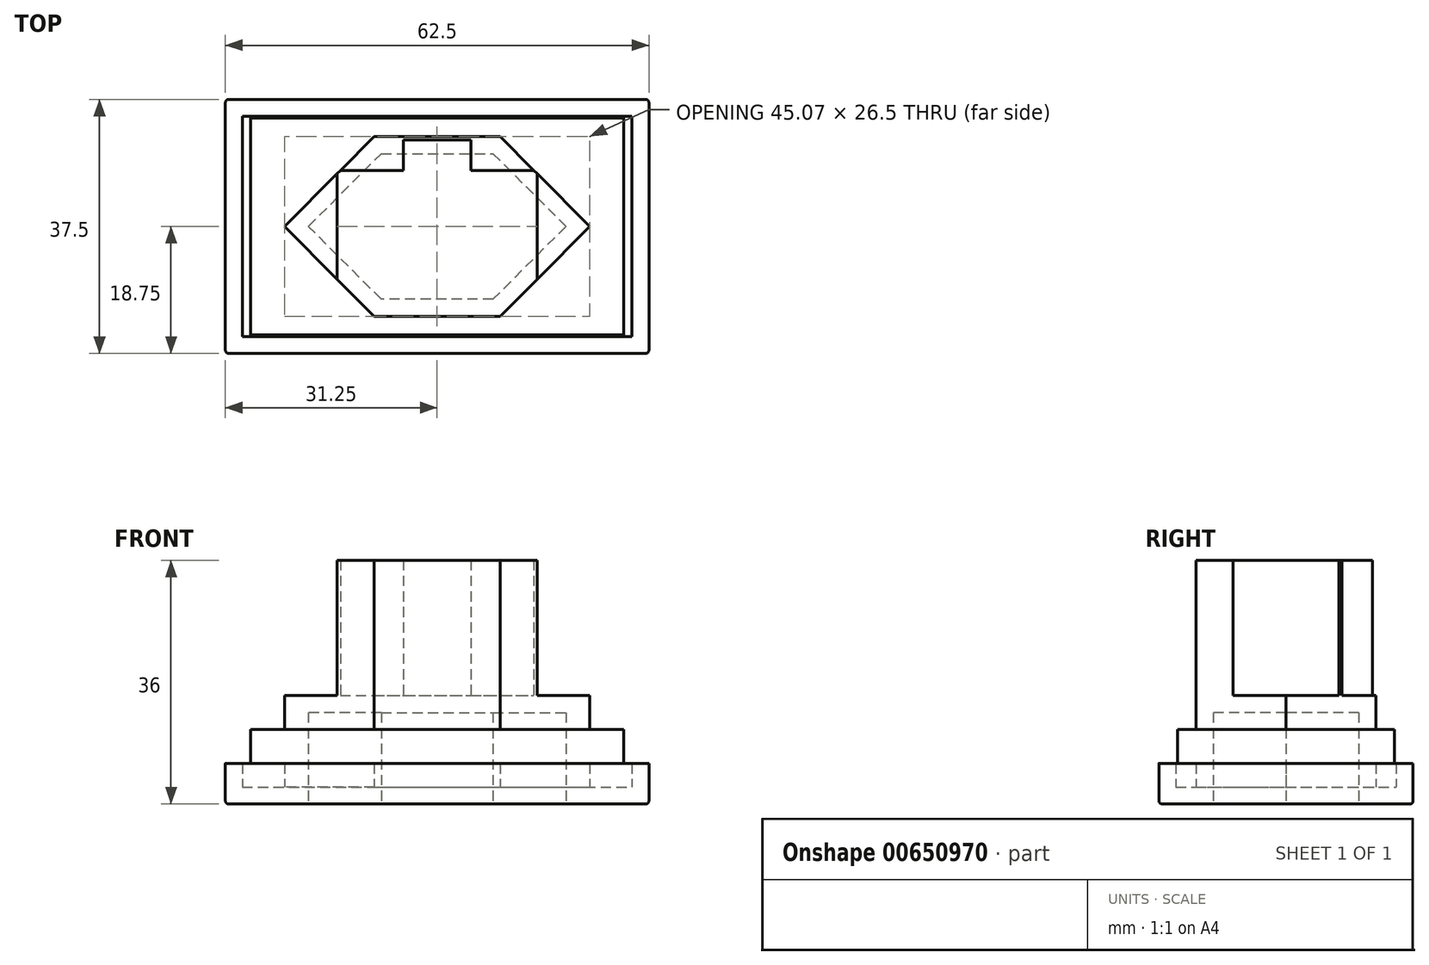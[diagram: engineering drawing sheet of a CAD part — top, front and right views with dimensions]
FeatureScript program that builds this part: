
annotation { "Feature Type Name" : "Feature", "Feature Type Description" : "" }
export const myFeature = defineFeature(function(context is Context, id is Id, definition is map)
    precondition{}
    {
        {
            var Q0;
            Q0=qCreatedBy(makeId("Top.planeOp"),FACE);
            var sketch = newSketch(context, id + "F0", { "sketchPlane" : qUnion([Q0])});
            skLineSegment(sketch, "E0.bottom", {"start": v(0, 0) * mm, "end": v(62.5, 0) * mm});
            skLineSegment(sketch, "E0.top", {"start": v(0, 37.5) * mm, "end": v(62.5, 37.5) * mm});
            skLineSegment(sketch, "E0.left", {"start": v(0, 0) * mm, "end": v(0, 37.5) * mm});
            skLineSegment(sketch, "E0.right", {"start": v(62.5, 0) * mm, "end": v(62.5, 37.5) * mm});
            skLineSegment(sketch, "E1", {"start": v(12.25, 18.75) * mm, "end": v(23, 29.5) * mm});
            skLineSegment(sketch, "E2", {"start": v(23, 29.5) * mm, "end": v(39.5, 29.5) * mm});
            skLineSegment(sketch, "E3", {"start": v(39.5, 29.5) * mm, "end": v(50.25, 18.75) * mm});
            skLineSegment(sketch, "E4", {"start": v(50.25, 18.75) * mm, "end": v(39.5, 8) * mm});
            skLineSegment(sketch, "E5", {"start": v(39.5, 8) * mm, "end": v(23, 8) * mm});
            skLineSegment(sketch, "E6", {"start": v(23, 8) * mm, "end": v(12.25, 18.75) * mm});
            skLineSegment(sketch, "E7", {"start": v(23, 8) * mm, "end": v(23, 29.5) * mm, "construction": true});
            skLineSegment(sketch, "E8", {"start": v(31.25, 29.5) * mm, "end": v(31.25, 8) * mm, "construction": true});
            skLineSegment(sketch, "E9", {"start": v(12.25, 18.75) * mm, "end": v(50.25, 18.75) * mm, "construction": true});
            skSolve(sketch);
        }
        {
            var Q0;
            Q0=makeQuery(id+"F0.imprint","IMPRINT",FACE,{"disambiguationData":[TD([[makeQuery(id+"F0.imprint","IMPRINT",EDGE,{"derivedFrom":sQuery(id+"F0.wireOp",EDGE,"E0.bottom")}),1.0]])]});
            extrude(context, id + "F1", {"entities" : qUnion([Q0]), "depth" : 6 * mm, "offsetDistance" : 25 * mm});
        }
        {
            var Q0;
            Q0=makeQuery(id+"F0.imprint","IMPRINT",FACE,{"disambiguationData":[TD([[makeQuery(id+"F0.imprint","IMPRINT",EDGE,{"derivedFrom":sQuery(id+"F0.wireOp",EDGE,"E1")}),-1.0]])]});
            extrude(context, id + "F2", {"entities" : qUnion([Q0]), "depth" : 13.5 * mm, "offsetDistance" : 25 * mm});
        }
        {
            var Q0;
            Q0=makeQuery(id+"F2.opExtrude","CAP_FACE",FACE,{"disambiguationData":[OSD([sQuery(id+"F0.wireOp",EDGE,"E1"),sQuery(id+"F0.wireOp",EDGE,"E2"),sQuery(id+"F0.wireOp",EDGE,"E3"),sQuery(id+"F0.wireOp",EDGE,"E4"),sQuery(id+"F0.wireOp",EDGE,"E5"),sQuery(id+"F0.wireOp",EDGE,"E6")])],"isStart":true});
            shell(context, id + "F3", {"entities" : qUnion([Q0]), "thickness" : 2.5 * mm, "oppositeDirection" : true});
        }
        {
            var Q0;
            Q0=makeQuery(id+"F1.opExtrude","CAP_FACE",FACE,{"disambiguationData":[OSD([sQuery(id+"F0.wireOp",EDGE,"E0.bottom"),sQuery(id+"F0.wireOp",EDGE,"E0.top"),sQuery(id+"F0.wireOp",EDGE,"E0.left"),sQuery(id+"F0.wireOp",EDGE,"E0.right"),sQuery(id+"F0.wireOp",EDGE,"E1"),sQuery(id+"F0.wireOp",EDGE,"E2"),sQuery(id+"F0.wireOp",EDGE,"E3"),sQuery(id+"F0.wireOp",EDGE,"E4"),sQuery(id+"F0.wireOp",EDGE,"E5"),sQuery(id+"F0.wireOp",EDGE,"E6")])],"isStart":false});
            shell(context, id + "F4", {"entities" : qUnion([Q0]), "thickness" : 2.5 * mm});
        }
        {
            var Q0;
            Q0=makeQuery(id+"F2.opExtrude","CAP_FACE",FACE,{"disambiguationData":[OSD([sQuery(id+"F0.wireOp",EDGE,"E1"),sQuery(id+"F0.wireOp",EDGE,"E2"),sQuery(id+"F0.wireOp",EDGE,"E3"),sQuery(id+"F0.wireOp",EDGE,"E4"),sQuery(id+"F0.wireOp",EDGE,"E5"),sQuery(id+"F0.wireOp",EDGE,"E6")])],"isStart":false});
            var sketch = newSketch(context, id + "F5", { "sketchPlane" : qUnion([Q0])});
            skLineSegment(sketch, "E10.bottom", {"start": v(16.5, 5.5) * mm, "end": v(46, 5.5) * mm});
            skLineSegment(sketch, "E10.left", {"start": v(16.5, 5.5) * mm, "end": v(16.5, 27) * mm});
            skLineSegment(sketch, "E10.right", {"start": v(46, 5.5) * mm, "end": v(46, 27) * mm});
            skLineSegment(sketch, "E11.top", {"start": v(26.25, 31.5) * mm, "end": v(36.25, 31.5) * mm});
            skLineSegment(sketch, "E11.left", {"start": v(26.25, 27) * mm, "end": v(26.25, 31.5) * mm});
            skLineSegment(sketch, "E11.right", {"start": v(36.25, 27) * mm, "end": v(36.25, 31.5) * mm});
            skLineSegment(sketch, "E12", {"start": v(16.5, 27) * mm, "end": v(26.25, 27) * mm});
            skLineSegment(sketch, "E13", {"start": v(36.25, 27) * mm, "end": v(46, 27) * mm});
            skLineSegment(sketch, "E14", {"start": v(31.25, 31.5) * mm, "end": v(31.25, 5.5) * mm, "construction": true});
            skSolve(sketch);
        }
        {
            var Q0;
            Q0=makeQuery(id+"F5.imprint","IMPRINT",FACE,{"disambiguationData":[TD([[makeQuery(id+"F5.imprint","IMPRINT",EDGE,{"derivedFrom":sQuery(id+"F5.wireOp",EDGE,"E11.top")}),-1.0]])]});
            extrude(context, id + "F6", {"entities" : qUnion([Q0]), "operationType" : NewBodyOperationType.ADD, "depth" : 20 * mm, "offsetDistance" : 25 * mm});
        }
        {
            var Q0;
            Q0=makeQuery(id+"F1.opExtrude","CAP_FACE",FACE,{"disambiguationData":[OSD([sQuery(id+"F0.wireOp",EDGE,"E0.bottom"),sQuery(id+"F0.wireOp",EDGE,"E0.top"),sQuery(id+"F0.wireOp",EDGE,"E0.left"),sQuery(id+"F0.wireOp",EDGE,"E0.right"),sQuery(id+"F0.wireOp",EDGE,"E1"),sQuery(id+"F0.wireOp",EDGE,"E2"),sQuery(id+"F0.wireOp",EDGE,"E3"),sQuery(id+"F0.wireOp",EDGE,"E4"),sQuery(id+"F0.wireOp",EDGE,"E5"),sQuery(id+"F0.wireOp",EDGE,"E6")])],"isStart":true});
            var Q1;
            Q1=makeQuery(id+"F1.opExtrude","SWEPT_EDGE",EDGE,{"disambiguationData":[OSD([sQuery(id+"F0.wireOp",EDGE,"E0.top"),sQuery(id+"F0.wireOp",EDGE,"E0.right")])]});
            var Q2;
            Q2=makeQuery(id+"F1.opExtrude","SWEPT_EDGE",EDGE,{"disambiguationData":[OSD([sQuery(id+"F0.wireOp",EDGE,"E0.top"),sQuery(id+"F0.wireOp",EDGE,"E0.left")])]});
            var Q3;
            Q3=makeQuery(id+"F1.opExtrude","SWEPT_EDGE",EDGE,{"disambiguationData":[OSD([sQuery(id+"F0.wireOp",EDGE,"E0.bottom"),sQuery(id+"F0.wireOp",EDGE,"E0.left")])]});
            var Q4;
            Q4=makeQuery(id+"F1.opExtrude","SWEPT_EDGE",EDGE,{"disambiguationData":[OSD([sQuery(id+"F0.wireOp",EDGE,"E0.bottom"),sQuery(id+"F0.wireOp",EDGE,"E0.right")])]});
            fillet(context, id + "F7", {"entities" : qUnion([Q0, Q1, Q2, Q3, Q4]), "radius" : 0.5 * mm, "tangentPropagation" : true, "allowEdgeOverflow" : false});
        }
        {
            var Q0;
            Q0=makeQuery(id+"F0.imprint","IMPRINT",FACE,{"disambiguationData":[TD([[makeQuery(id+"F0.imprint","IMPRINT",EDGE,{"derivedFrom":sQuery(id+"F0.wireOp",EDGE,"E1")}),-1.0]])]});
            var sketch = newSketch(context, id + "F8", { "sketchPlane" : qUnion([Q0])});
            skCircle(sketch, "E15", {"center": v(21.75, 18.75) * mm, "radius": 2 * mm});
            skCircle(sketch, "E16", {"center": v(40.75, 18.75) * mm, "radius": 2 * mm});
            skCircle(sketch, "E17", {"center": v(31.25, 12.75) * mm, "radius": 2 * mm});
            skLineSegment(sketch, "E18", {"start": v(21.75, 18.75) * mm, "end": v(40.75, 18.75) * mm, "construction": true});
            skLineSegment(sketch, "E19", {"start": v(40.75, 18.75) * mm, "end": v(31.25, 12.75) * mm, "construction": true});
            skLineSegment(sketch, "E20", {"start": v(31.25, 12.75) * mm, "end": v(21.75, 18.75) * mm, "construction": true});
            skSolve(sketch);
        }
        {
            var Q0;
            Q0=sQuery(id+"F8.wireOp",VERTEX,"E18.start");
            var Q1;
            Q1=sQuery(id+"F8.wireOp",VERTEX,"E17.center");
            var Q2;
            Q2=sQuery(id+"F8.wireOp",VERTEX,"E18.end");
            var Q3;
            Q3=makeQuery(id+"F1.opExtrude","SWEPT_BODY",BODY,{"disambiguationData":[OSD([sQuery(id+"F0.wireOp",EDGE,"E0.bottom"),sQuery(id+"F0.wireOp",EDGE,"E0.top"),sQuery(id+"F0.wireOp",EDGE,"E0.left"),sQuery(id+"F0.wireOp",EDGE,"E0.right"),sQuery(id+"F0.wireOp",EDGE,"E1"),sQuery(id+"F0.wireOp",EDGE,"E2"),sQuery(id+"F0.wireOp",EDGE,"E3"),sQuery(id+"F0.wireOp",EDGE,"E4"),sQuery(id+"F0.wireOp",EDGE,"E5"),sQuery(id+"F0.wireOp",EDGE,"E6")])]});
            hole(context, id + "F9", {"style" : HoleStyle.SIMPLE, "endStyle" : HoleEndStyle.BLIND, "oppositeDirection" : true, "holeDiameter" : 4 * mm, "majorDiameter" : 5 * mm, "holeDepth" : 15 * mm, "isTappedThrough" : true, "tappedDepth" : 12 * mm, "tapClearance" : 3, "locations" : qUnion([Q0, Q1, Q2]), "scope" : qUnion([Q3])});
        }
        {
            var Q0;
            Q0=makeQuery(id+"F1.opExtrude","CAP_FACE",FACE,{"disambiguationData":[OSD([sQuery(id+"F0.wireOp",EDGE,"E0.bottom"),sQuery(id+"F0.wireOp",EDGE,"E0.top"),sQuery(id+"F0.wireOp",EDGE,"E0.left"),sQuery(id+"F0.wireOp",EDGE,"E0.right"),sQuery(id+"F0.wireOp",EDGE,"E1"),sQuery(id+"F0.wireOp",EDGE,"E2"),sQuery(id+"F0.wireOp",EDGE,"E3"),sQuery(id+"F0.wireOp",EDGE,"E4"),sQuery(id+"F0.wireOp",EDGE,"E5"),sQuery(id+"F0.wireOp",EDGE,"E6")])],"isStart":false});
            var sketch = newSketch(context, id + "F10", { "sketchPlane" : qUnion([Q0])});
            skLineSegment(sketch, "E21.bottom", {"start": v(3.75, 34.75) * mm, "end": v(58.75, 34.75) * mm});
            skLineSegment(sketch, "E21.top", {"start": v(3.75, 2.75) * mm, "end": v(58.75, 2.75) * mm});
            skLineSegment(sketch, "E21.left", {"start": v(3.75, 34.75) * mm, "end": v(3.75, 2.75) * mm});
            skLineSegment(sketch, "E21.right", {"start": v(58.75, 34.75) * mm, "end": v(58.75, 2.75) * mm});
            skLineSegment(sketch, "E22", {"start": v(31.25, 34.75) * mm, "end": v(31.25, 2.75) * mm, "construction": true});
            skLineSegment(sketch, "E23", {"start": v(3.75, 18.75) * mm, "end": v(58.75, 18.75) * mm, "construction": true});
            skSolve(sketch);
        }
        {
            var Q0;
            Q0=makeQuery(id+"F10.imprint","IMPRINT",FACE,{"disambiguationData":[TD([[makeQuery(id+"F10.imprint","IMPRINT",EDGE,{"derivedFrom":sQuery(id+"F10.wireOp",EDGE,"E21.bottom")}),-1.0]])]});
            extrude(context, id + "F11", {"entities" : qUnion([Q0]), "operationType" : NewBodyOperationType.ADD, "depth" : 5 * mm, "offsetDistance" : 25 * mm});
        }
    });
